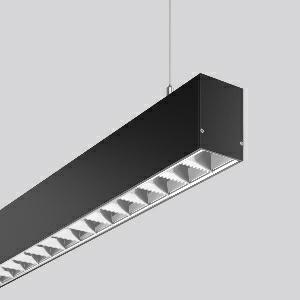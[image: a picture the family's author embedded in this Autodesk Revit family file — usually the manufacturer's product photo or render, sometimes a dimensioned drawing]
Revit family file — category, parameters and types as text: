
# Revit family: less_is_more_50_312338_003_1_4f15
name_source: partatom
category: Lighting Fixtures
units: mm (PartAtom-declared; Revit-internal decimal feet)

## family parameters
Cut with Voids When Loaded = No
Host = Face
Light Source = No
Part Type = Normal
Room Calculation Point = No
Round Connector Dimension = Use Diameter
Shared = No

## types (1)
- LESS IS MORE 50 (1 x LED Modul 840, 5300 lm, 4000)
    Apparent Load = 41 VA
    CIE Flux Codes = 95 100 100 100 100
    Color Rendering = 80
    Color Temperature = 4000
    Default Elevation = 1800 mm
    Description = Series: LESS IS MORE 50
Linear pendant luminaire for aesthetically sophisticated lighting. Housing: extruded aluminium profile, powder-coated. End cap aluminium powder-coated. Canopy made of aluminium, powder-coated. Alea optical system: Reflector structure (ABS, Aluminium-coated, highly polished) with integrated diffuser made of non-yellowing plastic (PMMA) opal for glare-free light at the workstation (screen-compliant according to EN 12464-1). Direct light emission. Suitable for pendant. 2-point steel cable suspension freely positionable and infinitely height-adjustable. Special lengths available on request. LED unit with integrated converter interchangeable and removable. Suitable for through-wiring. With sensors or as a safety luminaire on request. 
Colour: deep black, matt (RAL 9005)
Length: 1687 mm
Width: 57 mm
Height: 75 mm
Suspension length: 2000 mm
Lamp: LED
Socket: without socket
Colour temperature: 4000K
Colour rendering index (CRI): 80
System power: 41 W
Rated luminous flux: 5300 lm
Luminous efficiency: 129 lm/W
Control gear: Regulated power supply
Protection class: I
Type of protection: IP 20
    Height = 75 mm
    Lamp = 1 x LED Modul 840
    Lamp Light Flux = 5300 lm
    Lamp count = 1
    Length = 1687 mm
    Lifetime = 50000 h
    Luminous efficacy = 129 lm/W
    Manufacturer = RZB
    ModVariant = No
    Model = 312338.003.1
    Mounting Place = Ceiling
    Mounting Type = Pendant
    Number of Poles = 1
    OnlyDefault = Yes
    Power Factor = 1
    Product Name = LESS IS MORE 50
    Product group = Pendant LED linear luminaires
    ProductGroupID = 907
    Protection Class = Protection class I
    Protection Degree = IP 20
    RLX_Detail_Level = 1
    RLX_Emergency_Light_Flux = 0 lm
    RLX_Emergency_Type = 0
    RLX_Emergency_Type_DB = No
    RlxData = <blob elided: 39561 chars, md5=e114d6e8>
    Socket = socket
    Standby Power = 0 W
    System Light Flux = 5300 lm
    System Power = 41 W
    Type Comments = Product without accessories
    Type Image = 312342.003.jpg
    URL = http://relux.com
    VarID = ---
    Voltage = 230 V
    Voltage Range = 220-240 V
    Weight = 0.00 kg
    Width = 57 mm

## geometry (parser evidence)
native form markers: Blend x4, Sweep x9
no freeform markers — native parametric forms only
